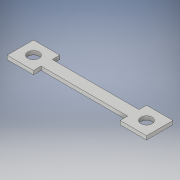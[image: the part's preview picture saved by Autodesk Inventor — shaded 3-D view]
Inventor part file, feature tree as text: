
AUTODESK INVENTOR PART (.ipt)
format: ipt  version: 2018 (Build 220112000, 112)  size: 138,240 bytes
history: native  units: in
note: dims shown in document units (in); Inventor stores cm internally (conversion verified against a paired STEP export)
features: extrude x3, sketch x3
ambient origin geometry x8: Origin, YZ Plane, XZ Plane, XY Plane, X Axis, Y Axis, Z Axis, Center Point
bodies: Solid1 (feature_tree)
feature tree (6):
  extrude  "Extrusion1"  Depth=1.4567in
  extrude  "Extrusion2"  Depth=0.2756in
  extrude  "Extrusion3"  TaperAngle=0.0deg  [1 undecoded]
  sketch  "Sketch1"  dims[d0=0.1181in d1=1.4567in]
  sketch  "Sketch2"  dims[d2=0.0394in d3=0.0in d4=0.2756in]
  sketch  "Sketch3"  dims[d5=0.2756in d6=0.0in d7=0.2756in d8=0.2756in d9=0.0in d12=0.0394in d13=0.0in d14=0.1181in d15=0.1181in d16=0.1181in d17=0.0in]
note: 1 required parameter value undecoded (feature->parameter linkage not recoverable at this tier; creation-order binding heuristic only, values carry confidence <= 0.55)
